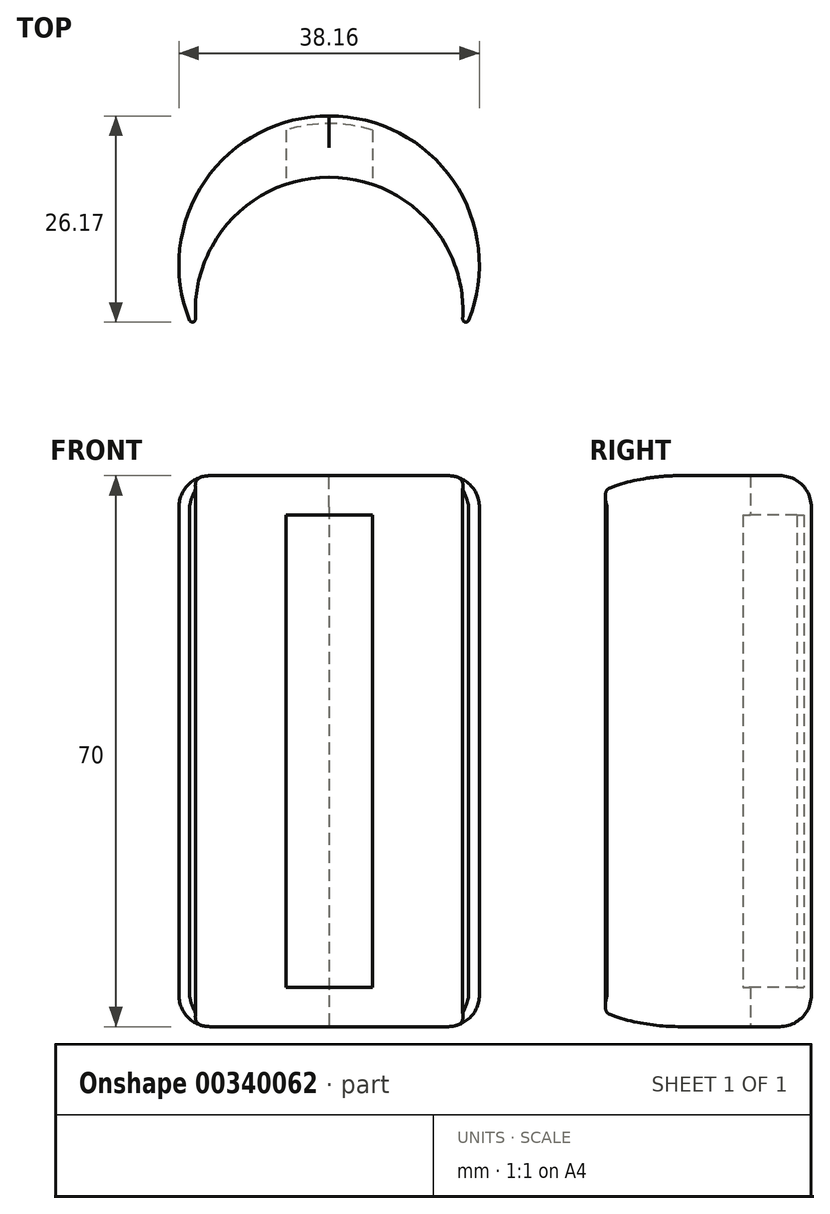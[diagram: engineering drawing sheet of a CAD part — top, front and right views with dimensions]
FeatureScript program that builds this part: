
annotation { "Feature Type Name" : "Feature", "Feature Type Description" : "" }
export const myFeature = defineFeature(function(context is Context, id is Id, definition is map)
    precondition{}
    {
        {
            var Q0;
            Q0=qCreatedBy(makeId("Top.planeOp"),FACE);
            var sketch = newSketch(context, id + "F0", { "sketchPlane" : qUnion([Q0])});
            skLineSegment(sketch, "E0", {"start": v(0, -3) * mm, "end": v(20.23, -3) * mm, "construction": true});
            skLineSegment(sketch, "E1", {"start": v(0, -3) * mm, "end": v(-16.85, -3) * mm, "construction": true});
            skLineSegment(sketch, "E2", {"start": v(0, -3) * mm, "end": v(0, -17.87) * mm, "construction": true});
            skArc(sketch, "E3", {"start": v(16.97, -1) * mm, "mid": v(17.27, -1.4) * mm, "end": v(17.72, -1.19) * mm});
            skArc(sketch, "E4.trimOffspring", {"start": v(16.97, -1) * mm, "mid": v(12.37, 11.66) * mm, "end": v(0, 17) * mm});
            skPoint(sketch, "E5.orphan", {"position": v(16.73, -3) * mm});
            skPoint(sketch, "E6.orphan", {"position": v(-16.73, -3) * mm});
            skLineSegment(sketch, "E7", {"start": v(0, -3) * mm, "end": v(0, 33.2) * mm, "construction": true});
            skLineSegment(sketch, "E8", {"start": v(3.83, -3) * mm, "end": v(3.83, 5.54) * mm, "construction": true});
            skLineSegment(sketch, "E9", {"start": v(3.83, 5.54) * mm, "end": v(0, 5.54) * mm, "construction": true});
            skArc(sketch, "E10.trimOffspring", {"start": v(17.72, -1.19) * mm, "mid": v(15.79, 16.51) * mm, "end": v(0, 24.75) * mm});
            skPoint(sketch, "E11.MirrorCS.end.orphan", {"position": v(-17.72, -1.19) * mm});
            skPoint(sketch, "E12.MirrorCS.end.orphan", {"position": v(0, 17) * mm});
            skPoint(sketch, "E12.MirrorCS.start.orphan", {"position": v(-16.97, -1) * mm});
            skArc(sketch, "E13.MirrorCS", {"start": v(-17.72, -1.19) * mm, "mid": v(-15.79, 16.51) * mm, "end": v(0, 24.75) * mm});
            skArc(sketch, "E14.MirrorCS", {"start": v(-16.97, -1) * mm, "mid": v(-12.37, 11.66) * mm, "end": v(0, 17) * mm});
            skArc(sketch, "E15.MirrorCS", {"start": v(-16.97, -1) * mm, "mid": v(-17.27, -1.4) * mm, "end": v(-17.72, -1.19) * mm});
            skSolve(sketch);
        }
        {
            var Q0;
            Q0=makeQuery(id+"F0.imprint","IMPRINT",FACE,{"disambiguationData":[TD([[makeQuery(id+"F0.imprint","IMPRINT",EDGE,{"derivedFrom":sQuery(id+"F0.wireOp",EDGE,"E3")}),1.0]])]});
            extrude(context, id + "F1", {"entities" : qUnion([Q0]), "endBound" : BoundingType.SYMMETRIC, "depth" : 70 * mm});
        }
        {
            var Q0;
            Q0=qCreatedBy(makeId("Top.planeOp"),FACE);
            var sketch = newSketch(context, id + "F2", { "sketchPlane" : qUnion([Q0])});
            skArc(sketch, "E16.0", {"start": v(-17.72, -1.19) * mm, "mid": v(-15.79, 16.51) * mm, "end": v(0, 24.75) * mm});
            skArc(sketch, "E16.1", {"start": v(17.72, -1.19) * mm, "mid": v(15.79, 16.51) * mm, "end": v(0, 24.75) * mm});
            skArc(sketch, "E17", {"start": v(5.5, 22.95) * mm, "mid": v(2.78, 23.59) * mm, "end": v(0, 23.8) * mm});
            skLineSegment(sketch, "E18", {"start": v(5.5, 22.95) * mm, "end": v(5.5, 12.95) * mm});
            skLineSegment(sketch, "E19", {"start": v(5.5, 12.95) * mm, "end": v(0, 12.95) * mm});
            skArc(sketch, "E20.MirrorCS", {"start": v(-5.5, 22.95) * mm, "mid": v(-2.78, 23.59) * mm, "end": v(0, 23.8) * mm});
            skLineSegment(sketch, "E21.MirrorCS", {"start": v(-5.5, 22.95) * mm, "end": v(-5.5, 12.95) * mm});
            skLineSegment(sketch, "E22.MirrorCS", {"start": v(-5.5, 12.95) * mm, "end": v(0, 12.95) * mm});
            skPoint(sketch, "E23.orphan", {"position": v(5.5, 25.88) * mm});
            skPoint(sketch, "E24.orphan", {"position": v(-5.5, 25.88) * mm});
            skSolve(sketch);
        }
        {
            var Q0;
            Q0 = qSketchRegion(id + "F2", true);
            extrude(context, id + "F3", {"entities" : qUnion([Q0]), "operationType" : NewBodyOperationType.REMOVE, "endBound" : BoundingType.SYMMETRIC, "depth" : 60 * mm});
        }
        {
            var Q0;
            Q0=makeQuery(id+"F1.opExtrude","CAP_EDGE",EDGE,{"disambiguationData":[OSD([sQuery(id+"F0.wireOp",EDGE,"E10.trimOffspring")])],"isStart":false});
            var Q1;
            Q1=makeQuery(id+"F1.opExtrude","CAP_EDGE",EDGE,{"disambiguationData":[OSD([sQuery(id+"F0.wireOp",EDGE,"E13.MirrorCS")])],"isStart":false});
            var Q2;
            Q2=makeQuery(id+"F1.opExtrude","CAP_EDGE",EDGE,{"disambiguationData":[OSD([sQuery(id+"F0.wireOp",EDGE,"E13.MirrorCS")])],"isStart":true});
            var Q3;
            Q3=makeQuery(id+"F1.opExtrude","CAP_EDGE",EDGE,{"disambiguationData":[OSD([sQuery(id+"F0.wireOp",EDGE,"E10.trimOffspring")])],"isStart":true});
            fillet(context, id + "F4", {"entities" : qUnion([Q0, Q1, Q2, Q3]), "radius" : 4 * mm, "tangentPropagation" : true, "allowEdgeOverflow" : false});
        }
    });
